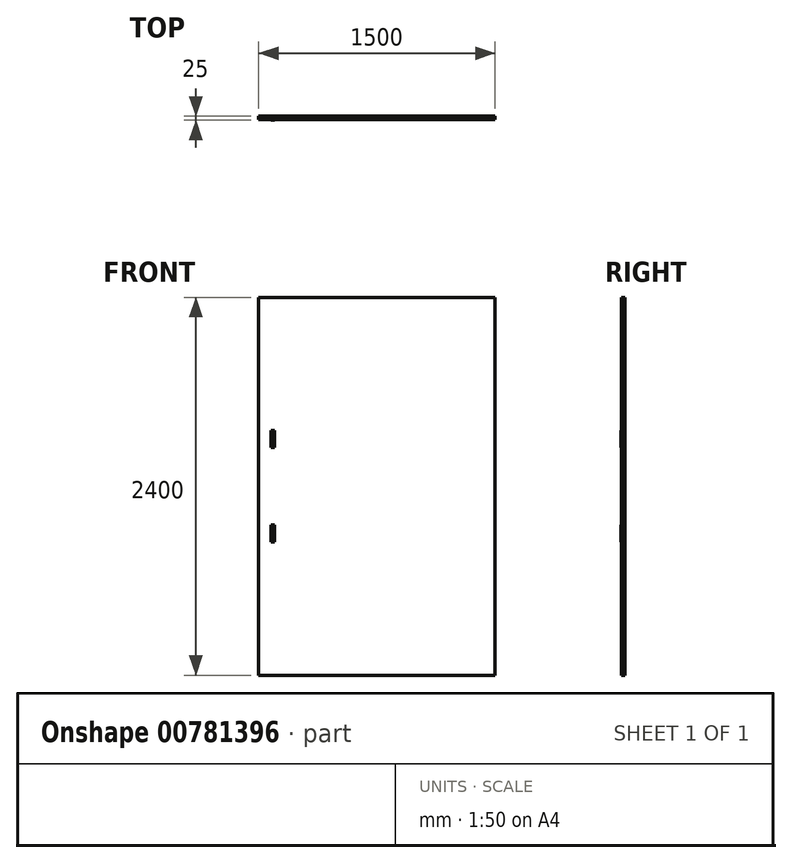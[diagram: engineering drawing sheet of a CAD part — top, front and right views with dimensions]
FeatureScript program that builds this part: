
annotation { "Feature Type Name" : "Feature", "Feature Type Description" : "" }
export const myFeature = defineFeature(function(context is Context, id is Id, definition is map)
    precondition{}
    {
        {
            var Q0;
            Q0=qCreatedBy(makeId("Front.planeOp"),FACE);
            var sketch = newSketch(context, id + "F0", { "sketchPlane" : qUnion([Q0])});
            skLineSegment(sketch, "E0.bottom", {"start": v(-750, 1200) * mm, "end": v(750, 1200) * mm});
            skLineSegment(sketch, "E0.top", {"start": v(-750, -1200) * mm, "end": v(750, -1200) * mm});
            skLineSegment(sketch, "E0.left", {"start": v(-750, 1200) * mm, "end": v(-750, -1200) * mm});
            skLineSegment(sketch, "E0.right", {"start": v(750, 1200) * mm, "end": v(750, -1200) * mm});
            skPoint(sketch, "E0.middle", {"position": v(0, 0) * mm});
            skSolve(sketch);
        }
        {
            var Q0;
            Q0 = qSketchRegion(id + "F0", true);
            extrude(context, id + "F1", {"entities" : qUnion([Q0]), "depth" : 20 * mm, "offsetDistance" : 25 * mm});
        }
        {
            var Q0;
            Q0=makeQuery(id+"F1.opExtrude","CAP_FACE",FACE,{"disambiguationData":[OSD([sQuery(id+"F0.wireOp",EDGE,"E0.bottom"),sQuery(id+"F0.wireOp",EDGE,"E0.top"),sQuery(id+"F0.wireOp",EDGE,"E0.left"),sQuery(id+"F0.wireOp",EDGE,"E0.right")])],"isStart":false});
            var sketch = newSketch(context, id + "F2", { "sketchPlane" : qUnion([Q0])});
            skLineSegment(sketch, "E1", {"start": v(-750, 0) * mm, "end": v(-660.17, 0) * mm, "construction": true});
            skLineSegment(sketch, "E2", {"start": v(-660.17, 0) * mm, "end": v(-660.17, 300) * mm, "construction": true});
            skLineSegment(sketch, "E3.bottom", {"start": v(-671.17, 355) * mm, "end": v(-649.17, 355) * mm});
            skLineSegment(sketch, "E3.top", {"start": v(-671.17, 245) * mm, "end": v(-649.17, 245) * mm});
            skLineSegment(sketch, "E3.left", {"start": v(-671.17, 355) * mm, "end": v(-671.17, 245) * mm});
            skLineSegment(sketch, "E3.right", {"start": v(-649.17, 355) * mm, "end": v(-649.17, 245) * mm});
            skPoint(sketch, "E3.middle", {"position": v(-660.17, 300) * mm});
            skLineSegment(sketch, "E4.MirrorCS", {"start": v(-649.17, -355) * mm, "end": v(-649.17, -245) * mm});
            skLineSegment(sketch, "E5.MirrorCS", {"start": v(-671.17, -355) * mm, "end": v(-671.17, -245) * mm});
            skLineSegment(sketch, "E6.MirrorCS", {"start": v(-671.17, -245) * mm, "end": v(-649.17, -245) * mm});
            skLineSegment(sketch, "E7.MirrorCS", {"start": v(-671.17, -355) * mm, "end": v(-649.17, -355) * mm});
            skSolve(sketch);
        }
        {
            var Q0;
            Q0 = qSketchRegion(id + "F2", true);
            extrude(context, id + "F3", {"entities" : qUnion([Q0]), "operationType" : NewBodyOperationType.ADD, "depth" : 5 * mm, "offsetDistance" : 25 * mm});
        }
    });
